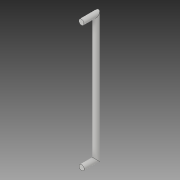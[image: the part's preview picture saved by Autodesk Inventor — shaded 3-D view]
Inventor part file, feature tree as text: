
AUTODESK INVENTOR PART (.ipt)
format: ipt  version: 2017 (Build 210142000, 142)  size: 76,800 bytes
history: native  units: mm
features: sketch x2, plane x1, sweep x1
ambient origin geometry x8: Origin, YZ Plane, XZ Plane, XY Plane, X Axis, Y Axis, Z Axis, Center Point
bodies: Solid1 (feature_tree)
feature tree (4):
  sketch  "Sketch1"  dims[d0=431.8mm d1=-50.0mm]
  plane  "Work Plane1"
  sweep  "Sweep1"
  sketch  "Sketch2"  dims[d2=18.0mm d3=0.0mm d4=0.0mm]
